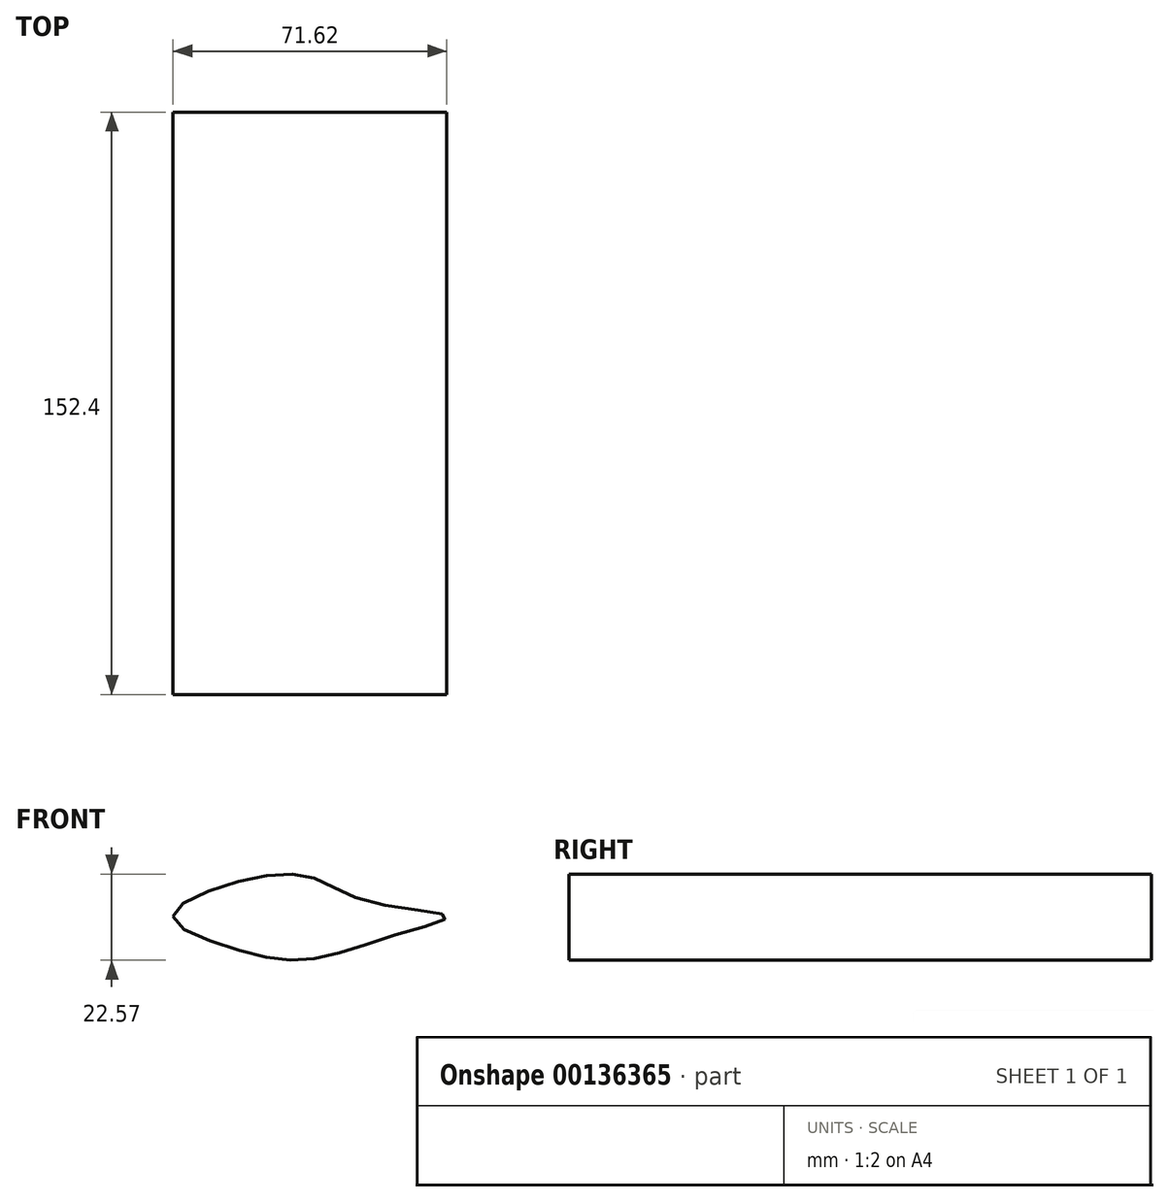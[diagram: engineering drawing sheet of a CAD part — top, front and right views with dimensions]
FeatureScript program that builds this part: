
annotation { "Feature Type Name" : "Feature", "Feature Type Description" : "" }
export const myFeature = defineFeature(function(context is Context, id is Id, definition is map)
    precondition{}
    {
        {
            var Q0;
            Q0=qCreatedBy(makeId("Front.planeOp"),FACE);
            var sketch = newSketch(context, id + "F0", { "sketchPlane" : qUnion([Q0])});
            skFitSpline(sketch, "E0", {"points": [v(-33.37, 0) * mm, v(-17.97, 8.7) * mm, v(2.28, 10.41) * mm, v(17.97, 3.85) * mm, v(38.22, 0) * mm, v(24.25, -5) * mm, v(2, -11.27) * mm, v(-17.4, -8.41) * mm, v(-33.37, 0) * mm]});
            skSolve(sketch);
        }
        {
            var Q0;
            Q0 = qSketchRegion(id + "F0", true);
            extrude(context, id + "F1", {"entities" : qUnion([Q0]), "depth" : 152.4 * mm});
        }
    });
